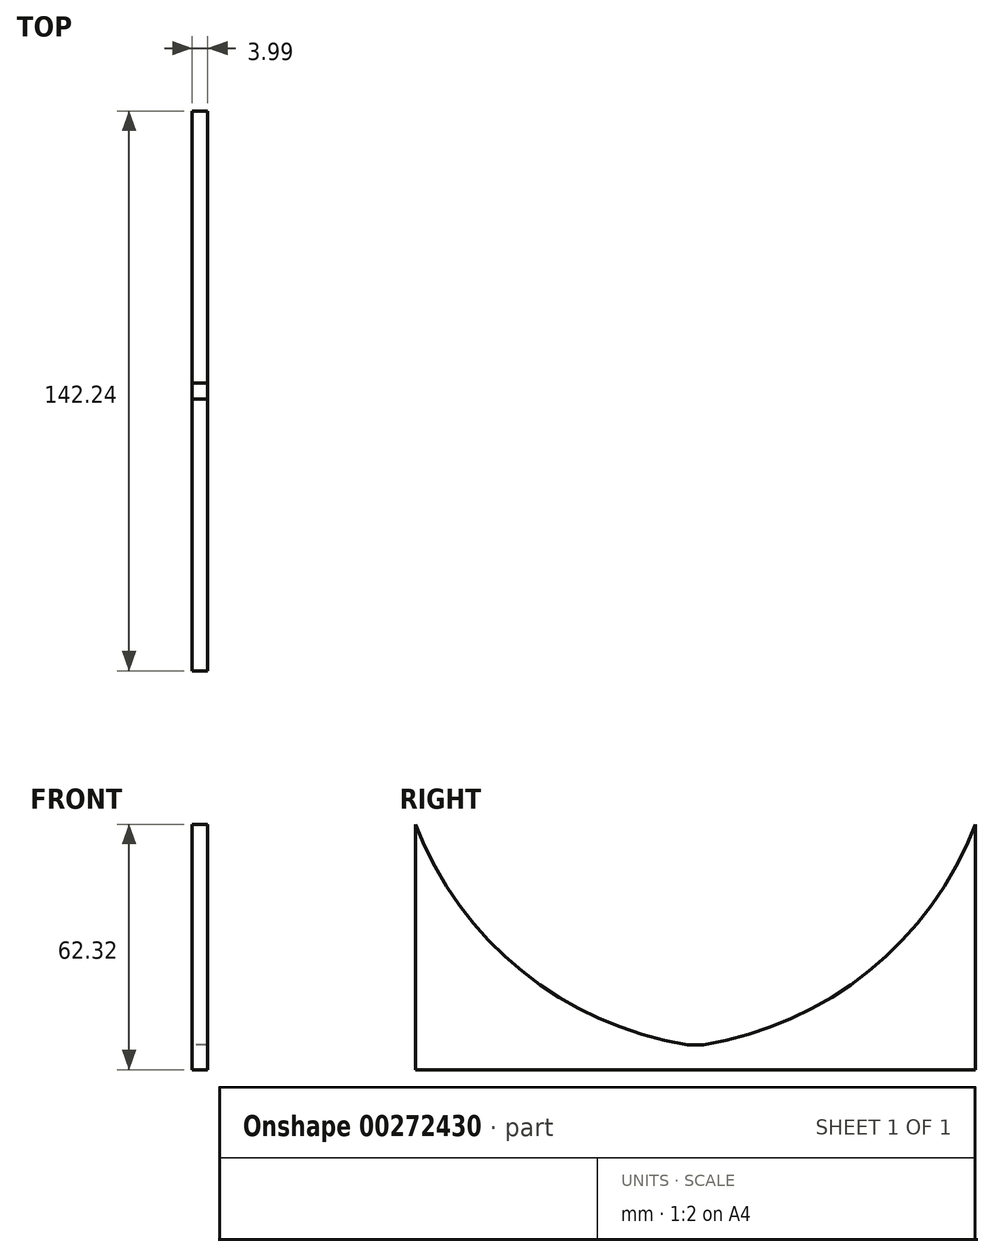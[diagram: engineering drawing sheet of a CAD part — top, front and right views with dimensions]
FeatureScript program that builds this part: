
annotation { "Feature Type Name" : "Feature", "Feature Type Description" : "" }
export const myFeature = defineFeature(function(context is Context, id is Id, definition is map)
    precondition{}
    {
        {
            var Q0;
            Q0=qCreatedBy(makeId("Right.planeOp"),FACE);
            var sketch = newSketch(context, id + "F0", { "sketchPlane" : qUnion([Q0])});
            skLineSegment(sketch, "E0", {"start": v(-2, 0) * mm, "end": v(-2, 6.35) * mm});
            skLineSegment(sketch, "E1", {"start": v(-2, 6.35) * mm, "end": v(2, 6.35) * mm});
            skLineSegment(sketch, "E2", {"start": v(2, 6.35) * mm, "end": v(2, 0) * mm});
            skArc(sketch, "E3", {"start": v(2, 6.35) * mm, "mid": v(44.06, 25.07) * mm, "end": v(71.12, 62.32) * mm});
            skLineSegment(sketch, "E4", {"start": v(2, 0) * mm, "end": v(71.12, 0) * mm});
            skLineSegment(sketch, "E5", {"start": v(71.12, 0) * mm, "end": v(71.12, 62.32) * mm});
            skLineSegment(sketch, "E6", {"start": v(-2, 0) * mm, "end": v(-71.12, 0) * mm});
            skLineSegment(sketch, "E7", {"start": v(-71.12, 0) * mm, "end": v(-71.12, 62.32) * mm});
            skArc(sketch, "E8", {"start": v(-71.12, 62.32) * mm, "mid": v(-44.06, 25.07) * mm, "end": v(-2, 6.35) * mm});
            skLineSegment(sketch, "E9", {"start": v(-2, 0) * mm, "end": v(2, 0) * mm});
            skSolve(sketch);
        }
        {
            var Q0;
            Q0 = qSketchRegion(id + "F0", true);
            extrude(context, id + "F1", {"entities" : qUnion([Q0]), "depth" : 4 * mm});
        }
    });
